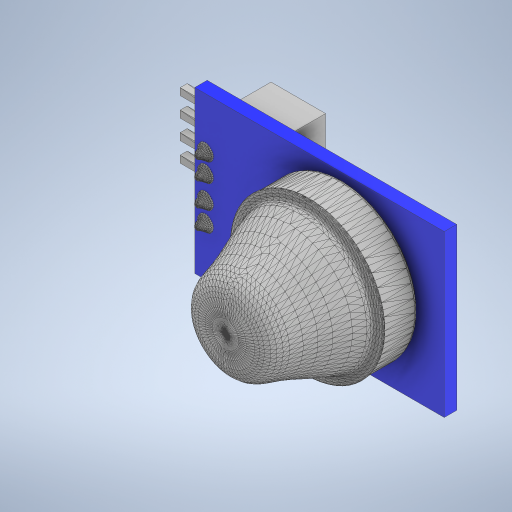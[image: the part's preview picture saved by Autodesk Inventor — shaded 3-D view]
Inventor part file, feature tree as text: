
AUTODESK INVENTOR PART (.ipt)
format: ipt  version: 2023 (Build 270158000, 158)  size: 7,833,088 bytes
history: mixed  units: in
note: dims shown in document units (in); Inventor stores cm internally (conversion verified against a paired STEP export)
features: other x54, extrude x2, sketch x2, imported_body x1
ambient origin geometry x8: Origin, YZ Plane, XZ Plane, XY Plane, X Axis, Y Axis, Z Axis, Center Point
bodies: Solid1 (imported_parasolid), Solid2 (imported_parasolid), Solid3 (imported_parasolid), Solid4 (imported_parasolid), Solid5 (imported_parasolid), Solid6 (imported_parasolid), Solid7 (imported_parasolid), Solid8 (imported_parasolid), Solid9 (imported_parasolid), Solid10 (imported_parasolid), Solid11 (imported_parasolid), Solid12 (imported_parasolid), Solid13 (imported_parasolid), Solid14 (imported_parasolid), Solid15 (imported_parasolid), Solid16 (imported_parasolid), Solid17 (imported_parasolid), Solid18 (imported_parasolid), Solid19 (imported_parasolid), Solid20 (imported_parasolid), Solid21 (imported_parasolid), Solid22 (imported_parasolid), Solid23 (imported_parasolid), Solid24 (imported_parasolid), Solid25 (imported_parasolid), Solid26 (imported_parasolid), Solid27 (imported_parasolid), Solid28 (imported_parasolid), Solid29 (imported_parasolid), Solid30 (imported_parasolid), Solid31 (imported_parasolid), Solid32 (imported_parasolid), Solid33 (imported_parasolid), Solid34 (imported_parasolid), Solid35 (imported_parasolid), Solid36 (imported_parasolid), Solid37 (imported_parasolid), Solid38 (imported_parasolid), Solid39 (imported_parasolid), Solid40 (imported_parasolid), Solid41 (imported_parasolid), Solid42 (imported_parasolid), Solid43 (imported_parasolid), Solid44 (imported_parasolid), Solid45 (imported_parasolid), Solid46 (imported_parasolid), Solid47 (imported_parasolid), Solid48 (imported_parasolid), Solid49 (imported_parasolid), Solid50 (imported_parasolid), Solid51 (imported_parasolid)
feature tree (59):
  other  "Repaired Geometry1"
  other  "Repaired Geometry2"
  extrude  "Extrusion1"  Depth=0.0394in TaperAngle=0.0deg
  extrude  "Extrusion2"  [1 undecoded]
  sketch  "Sketch1"  dims[d0=1.2598in d1=0.0in d2=0.0394in d3=0.0in]
  other  "MeshBody1"
  other  "MeshBody1 (1)"
  other  "MeshBody1 (2)"
  other  "MeshBody1 (3)"
  other  "MeshBody1 (4)"
  other  "MeshBody1 (5)"
  other  "MeshBody1 (6)"
  other  "MeshBody1 (7)"
  other  "MeshBody1 (8)"
  other  "MeshBody1 (9)"
  other  "MeshBody1 (10)"
  other  "MeshBody1 (11)"
  other  "MeshBody1 (12)"
  other  "MeshBody1 (13)"
  other  "MeshBody1 (14)"
  other  "MeshBody1 (15)"
  other  "MeshBody1 (16)"
  other  "MeshBody1 (17)"
  other  "MeshBody1 (18)"
  other  "MeshBody1 (19)"
  other  "MeshBody1 (20)"
  other  "MeshBody1 (21)"
  other  "MeshBody1 (22)"
  other  "MeshBody1 (23)"
  other  "MeshBody1 (24)"
  other  "MeshBody1 (25)"
  other  "MeshBody1 (26)"
  other  "MeshBody1 (27)"
  other  "MeshBody1 (28)"
  other  "MeshBody1 (29)"
  other  "MeshBody1 (30)"
  other  "MeshBody1 (31)"
  other  "MeshBody1 (32)"
  other  "MeshBody1 (33)"
  other  "MeshBody1 (34)"
  other  "MeshBody1 (35)"
  other  "MeshBody1 (36)"
  other  "MeshBody5"
  other  "MeshBody7"
  other  "MeshBody7 (1)"
  other  "MeshBody7 (2)"
  other  "MeshBody7 (3)"
  other  "MeshBody9"
  other  "MeshBody8"
  other  "MeshBody8 (1)"
  other  "MeshBody8 (2)"
  other  "MeshBody8 (3)"
  other  "MeshBody8 (4)"
  other  "MeshBody8 (5)"
  other  "MeshBody8 (6)"
  sketch  "Sketch2"
  other  "Composite1"
  other  "Srf1"
  imported_body  NMx_Import_Brep_tag  [imported B-rep: ~13167 faces, bbox_mm=[39.361894, 20.650001, 21.358295]]
note: 1 required parameter value undecoded (feature->parameter linkage not recoverable at this tier; creation-order binding heuristic only, values carry confidence <= 0.55)
